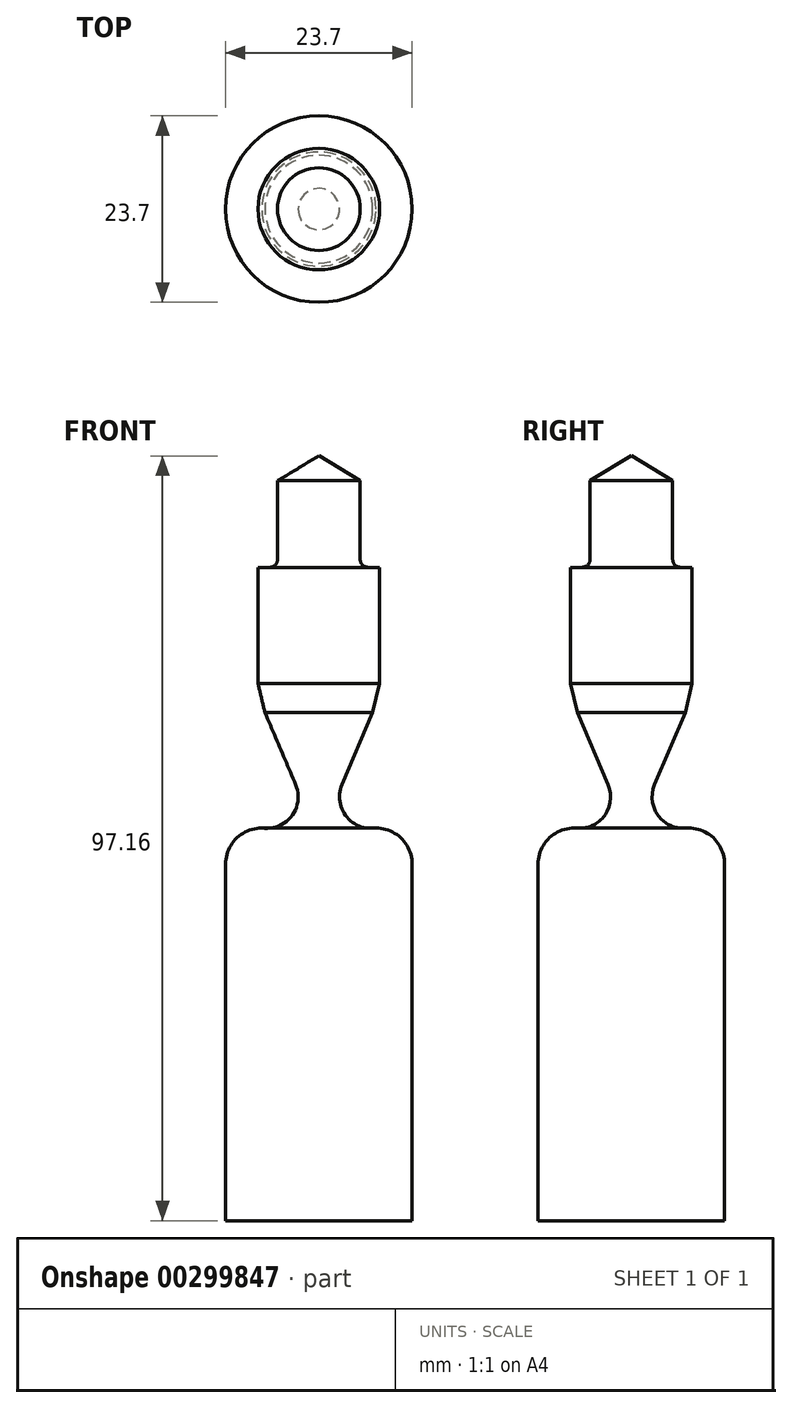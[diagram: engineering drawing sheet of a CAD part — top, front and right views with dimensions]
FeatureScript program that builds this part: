
annotation { "Feature Type Name" : "Feature", "Feature Type Description" : "" }
export const myFeature = defineFeature(function(context is Context, id is Id, definition is map)
    precondition{}
    {
        {
            var Q0;
            Q0=qCreatedBy(makeId("Front.planeOp"),FACE);
            var sketch = newSketch(context, id + "F0", { "sketchPlane" : qUnion([Q0])});
            skLineSegment(sketch, "E0", {"start": v(5.25, -6) * mm, "end": v(5.25, -6) * mm});
            skLineSegment(sketch, "E1", {"start": v(5.25, -6) * mm, "end": v(5.25, -16) * mm});
            skLineSegment(sketch, "E2", {"start": v(0, -100) * mm, "end": v(0, -100) * mm});
            skLineSegment(sketch, "E3", {"start": v(0, -100) * mm, "end": v(11.85, -100) * mm});
            skLineSegment(sketch, "E4", {"start": v(11.85, -100) * mm, "end": v(11.85, -100) * mm});
            skLineSegment(sketch, "E5", {"start": v(2.95, -44.6) * mm, "end": v(6.84, -35.46) * mm});
            skLineSegment(sketch, "E6", {"start": v(6.84, -35.46) * mm, "end": v(6.84, -35.46) * mm});
            skLineSegment(sketch, "E7", {"start": v(6.84, -35.46) * mm, "end": v(7.72, -31.77) * mm});
            skLineSegment(sketch, "E8", {"start": v(7.72, -31.77) * mm, "end": v(7.72, -17) * mm});
            skArc(sketch, "E9", {"start": v(2.95, -44.6) * mm, "mid": v(3.47, -48.62) * mm, "end": v(7.25, -50.11) * mm});
            skPoint(sketch, "E10.start.orphan", {"position": v(11.85, -50.11) * mm});
            skLineSegment(sketch, "E11", {"start": v(11.85, -100) * mm, "end": v(11.85, -54.71) * mm});
            skArc(sketch, "E12", {"start": v(11.85, -54.71) * mm, "mid": v(10.5, -51.46) * mm, "end": v(7.25, -50.11) * mm});
            skLineSegment(sketch, "E13", {"start": v(7.72, -17) * mm, "end": v(6.25, -17) * mm});
            skArc(sketch, "E14", {"start": v(5.25, -16) * mm, "mid": v(5.54, -16.71) * mm, "end": v(6.25, -17) * mm});
            skPoint(sketch, "E15.start.orphan", {"position": v(0, 0) * mm});
            skLineSegment(sketch, "E16", {"start": v(5.25, -6) * mm, "end": v(0, -2.84) * mm});
            skLineSegment(sketch, "E17", {"start": v(0, -2.84) * mm, "end": v(0, -2.84) * mm});
            skLineSegment(sketch, "E18", {"start": v(0, -100) * mm, "end": v(0, -2.84) * mm});
            skSolve(sketch);
        }
        {
            var Q0;
            Q0 = qSketchRegion(id + "F0", true);
            var Q1;
            Q1=sQuery(id+"F0.wireOp",EDGE,"E18");
            revolve(context, id + "F1", {"entities" : qUnion([Q0]), "axis" : qUnion([Q1]), "revolveType" : RevolveType.FULL});
        }
    });
